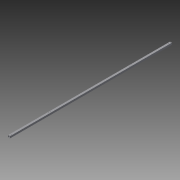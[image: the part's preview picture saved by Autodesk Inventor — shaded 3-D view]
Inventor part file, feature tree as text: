
AUTODESK INVENTOR PART (.ipt)
format: ipt  version: 2015 SP1 (Build 190203100, 203)  size: 107,520 bytes
history: native  units: in
note: dims shown in document units (in); Inventor stores cm internally (conversion verified against a paired STEP export)
features: extrude x2, sketch x2
ambient origin geometry x8: Origin, YZ Plane, XZ Plane, XY Plane, X Axis, Y Axis, Z Axis, Center Point
bodies: Solid1 (feature_tree)
feature tree (4):
  extrude  "Extrusion1"  Depth=0.9843in
  extrude  "Extrusion2"  Depth=84.252in TaperAngle=0.0deg
  sketch  "Sketch2"  dims[d0=0.9843in d1=0.9843in]
  sketch  "Sketch3"  dims[d3=0.1181in d4=84.252in d5=0.0in d6=0.2756in d7=0.4331in d8=0.7087in d9=19.4291in d10=0.9843in d11=0.9843in d12=41.1417in d13=0.7087in d14=19.4291in d16=0.0in d17=0.0in]
